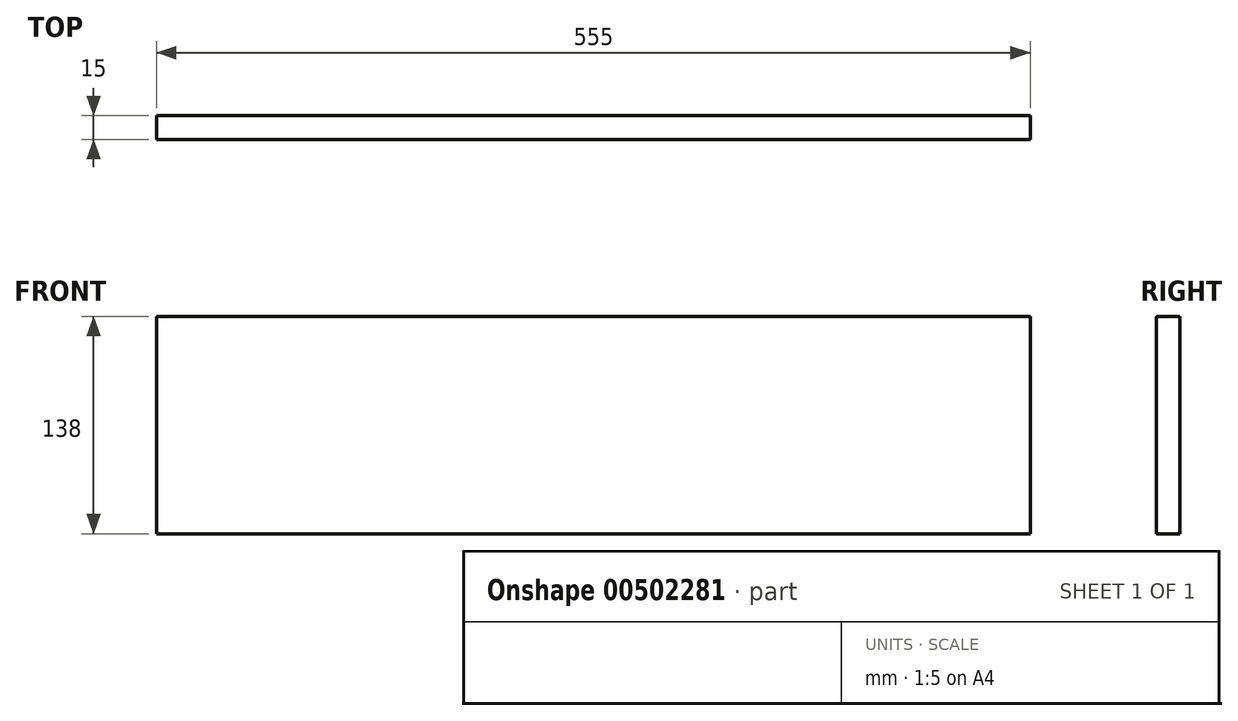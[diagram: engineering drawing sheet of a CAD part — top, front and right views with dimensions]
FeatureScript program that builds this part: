
annotation { "Feature Type Name" : "Feature", "Feature Type Description" : "" }
export const myFeature = defineFeature(function(context is Context, id is Id, definition is map)
    precondition{}
    {
        {
            var Q0;
            Q0=qCreatedBy(makeId("Front.planeOp"),FACE);
            var sketch = newSketch(context, id + "F0", { "sketchPlane" : qUnion([Q0])});
            skLineSegment(sketch, "E0.bottom", {"start": v(-1000, 69) * mm, "end": v(-445, 69) * mm});
            skLineSegment(sketch, "E0.top", {"start": v(-1000, -69) * mm, "end": v(-445, -69) * mm});
            skLineSegment(sketch, "E0.left", {"start": v(-1000, 69) * mm, "end": v(-1000, -69) * mm});
            skLineSegment(sketch, "E0.right", {"start": v(-445, 69) * mm, "end": v(-445, -69) * mm});
            skSolve(sketch);
        }
        {
            var Q0;
            Q0 = qSketchRegion(id + "F0", true);
            extrude(context, id + "F1", {"entities" : qUnion([Q0]), "depth" : 15 * mm});
        }
    });
